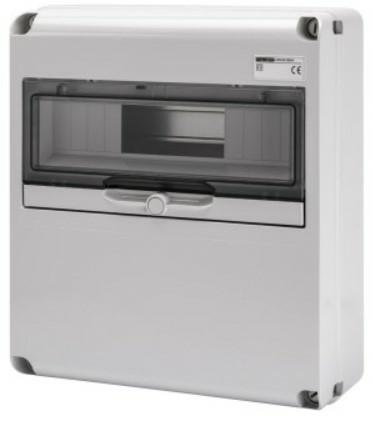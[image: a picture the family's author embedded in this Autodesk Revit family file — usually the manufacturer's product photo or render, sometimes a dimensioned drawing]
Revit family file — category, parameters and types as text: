
# Revit family: Building-IEC309Boards-GEWISS-68QDIN-DISTRIBUTION-BOARD-14MOD_BLANK
name_source: partatom
category: Apparecchi elettrici
units: mm (PartAtom-declared; Revit-internal decimal feet)

## family parameters
Condiviso = No
Host = Superficie
Mantenere orientamento annotazione = Sì
Punto di calcolo locali = Sì
Quota connettore circolare = Usa diametro
Taglio con vuoti quando caricato = No
Tipo di parte = Normale

## types (1)
- GW68004N - Q-DIN 14M.BLIND COV. 360X320X135 IP65
    Accordance with Standards = EN 60208 - EN 60670-1 - IEC 60670-24
    Catalogue = BUILDING
    Catalogue Range = 68 QDIN
    Colour = Grey RAL 7035
    Descrizione = Q-DIN 14M.BLIND COV. 360X320X135 IP65
    Dispersible power A (W) = 24
    Dispersible power B (W) = 64
    EAN code = 8011564744752
    Electrocod = 2242
    Glow Wire Test = 650°C
    Houseable socket = Blank lid
    IDF = a3353da9-37d5-4705-baba-cf205a3a377c
    IDT = d585780b-ac8c-4f69-a7b1-54dd751465a2
    IP degree = IP65
    Immagine tipo = GW68004N.jpg
    Installation type = Surface-mounting
    Insulation class = II
    L_Moduli = 266 mm  [stored 0.872703 ft]
    Modello = GW68004N
    N_Moduli = 14 mm  [stored 0.0459318 ft]
    No. of modules EN 50022 = 14
    No. of provided blank lids = -
    Operating temperature: = -25 +40 °C
    POMELLO = bianco
    PRESA = rosso
    Produttore = GEWISS S.p.A.
    Prospetto di default = 1219 mm
    SEO = Board
    STRUTTURA = RAL - 7035
    STRUTTURA ALTA = Poche
    Shock resistance = IK09
    Spostamento_S = 1000 mm  [stored 3.28084 ft]
    Technical sheet = https://www.gewiss.com
    Thermo-pressure with ball = 70
    URL = https://www.gewiss.com
    VETRO = Vetro
    Version file RFA = 21.5
    Version type = Empty

note: source unit labels omitted for Thermo-pressure with ball — the stored unit's dimension contradicts the parameter name (converter mislabeling)

note: [stored X ft] marks values corroborated as IEEE doubles in the binary element streams (Revit-internal decimal feet)

## geometry (parser evidence)
native form markers: Sweep x2
no freeform markers — native parametric forms only
